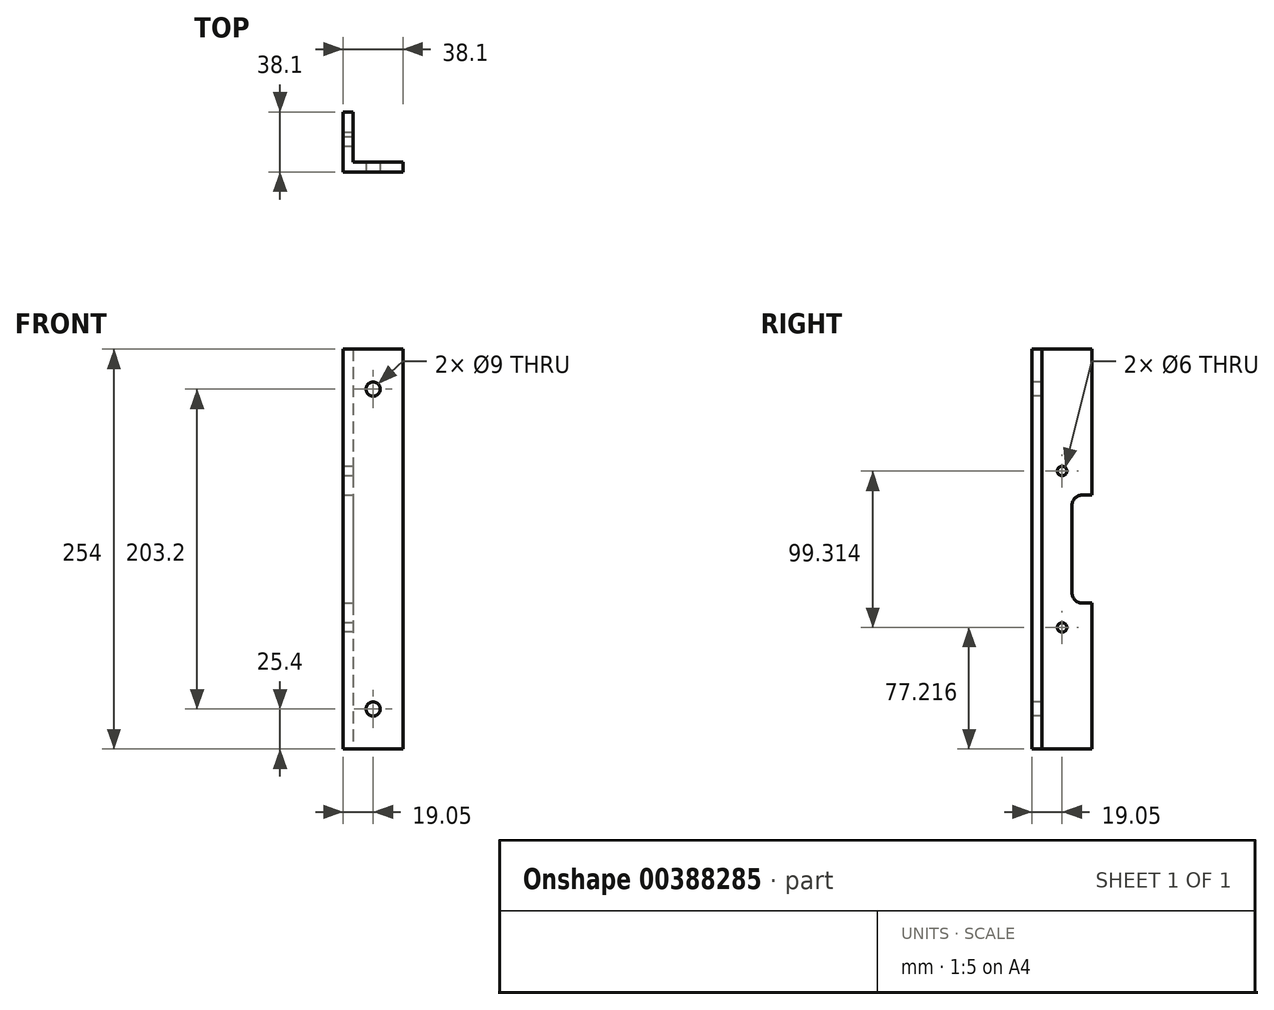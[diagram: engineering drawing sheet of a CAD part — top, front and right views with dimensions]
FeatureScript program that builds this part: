
annotation { "Feature Type Name" : "Feature", "Feature Type Description" : "" }
export const myFeature = defineFeature(function(context is Context, id is Id, definition is map)
    precondition{}
    {
        {
            var Q0;
            Q0=qCreatedBy(makeId("Top.planeOp"),FACE);
            var sketch = newSketch(context, id + "F0", { "sketchPlane" : qUnion([Q0])});
            skLineSegment(sketch, "E0", {"start": v(0, 0) * mm, "end": v(38.1, 0) * mm});
            skLineSegment(sketch, "E1", {"start": v(38.1, 0) * mm, "end": v(38.1, 6.35) * mm});
            skLineSegment(sketch, "E2", {"start": v(38.1, 6.35) * mm, "end": v(6.35, 6.35) * mm});
            skLineSegment(sketch, "E3", {"start": v(6.35, 6.35) * mm, "end": v(6.35, 38.1) * mm});
            skLineSegment(sketch, "E4", {"start": v(6.35, 38.1) * mm, "end": v(0, 38.1) * mm});
            skLineSegment(sketch, "E5", {"start": v(0, 38.1) * mm, "end": v(0, 0) * mm});
            skSolve(sketch);
        }
        {
            var Q0;
            Q0=makeQuery(id+"F0.imprint","IMPRINT",FACE,{"disambiguationData":[TD([[makeQuery(id+"F0.imprint","IMPRINT",EDGE,{"derivedFrom":sQuery(id+"F0.wireOp",EDGE,"E0")}),1.0]])]});
            extrude(context, id + "F1", {"entities" : qUnion([Q0]), "depth" : 254 * mm});
        }
        {
            var Q0;
            Q0=makeQuery(id+"F1.opExtrude","SWEPT_FACE",FACE,{"disambiguationData":[OSD([sQuery(id+"F0.wireOp",EDGE,"E0")])]});
            var sketch = newSketch(context, id + "F2", { "sketchPlane" : qUnion([Q0])});
            skLineSegment(sketch, "E6", {"start": v(19.05, 254) * mm, "end": v(19.05, 33.27) * mm, "construction": true});
            skPoint(sketch, "E7", {"position": v(19.05, 228.6) * mm});
            skPoint(sketch, "E8", {"position": v(19.05, 25.4) * mm});
            skSolve(sketch);
        }
        {
            var Q0;
            Q0=sQuery(id+"F2.wireOp",VERTEX,"E7");
            var Q1;
            Q1=makeQuery(id+"F1.opExtrude","SWEPT_BODY",BODY,{"disambiguationData":[OSD([sQuery(id+"F0.wireOp",EDGE,"E0"),sQuery(id+"F0.wireOp",EDGE,"E1"),sQuery(id+"F0.wireOp",EDGE,"E2"),sQuery(id+"F0.wireOp",EDGE,"E3"),sQuery(id+"F0.wireOp",EDGE,"E4"),sQuery(id+"F0.wireOp",EDGE,"E5")])]});
            hole(context, id + "F3", {"style" : HoleStyle.SIMPLE, "endStyle" : HoleEndStyle.THROUGH, "holeDiameter" : 9 * mm, "isTappedThrough" : true, "tappedDepth" : 12.7 * mm, "tapClearance" : 3, "locations" : qUnion([Q0]), "scope" : qUnion([Q1])});
        }
        {
            var Q0;
            Q0=sQuery(id+"F2.wireOp",VERTEX,"E8");
            var Q1;
            Q1=makeQuery(id+"F1.opExtrude","SWEPT_BODY",BODY,{"disambiguationData":[OSD([sQuery(id+"F0.wireOp",EDGE,"E0"),sQuery(id+"F0.wireOp",EDGE,"E1"),sQuery(id+"F0.wireOp",EDGE,"E2"),sQuery(id+"F0.wireOp",EDGE,"E3"),sQuery(id+"F0.wireOp",EDGE,"E4"),sQuery(id+"F0.wireOp",EDGE,"E5")])]});
            hole(context, id + "F4", {"style" : HoleStyle.SIMPLE, "endStyle" : HoleEndStyle.THROUGH, "holeDiameter" : 9 * mm, "isTappedThrough" : true, "tappedDepth" : 12.7 * mm, "tapClearance" : 3, "locations" : qUnion([Q0]), "scope" : qUnion([Q1])});
        }
        {
            var Q0;
            Q0=makeQuery(id+"F1.opExtrude","SWEPT_FACE",FACE,{"disambiguationData":[OSD([sQuery(id+"F0.wireOp",EDGE,"E5")])]});
            var sketch = newSketch(context, id + "F5", { "sketchPlane" : qUnion([Q0])});
            skLineSegment(sketch, "E9", {"start": v(-19.05, -96.16) * mm, "end": v(-19.05, 311.1) * mm, "construction": true});
            skSolve(sketch);
        }
        {
            var Q0;
            {var subQ0=sQuery(id+"F0.wireOp",EDGE,"E5");Q0=makeQuery(id+"F5.imprint","IMPRINT",FACE,{"disambiguationData":[TD([[makeQuery(id+"F5.imprint","IMPRINT",EDGE,{"derivedFrom":makeQuery(id+"F1.opExtrude","CAP_EDGE",EDGE,{"disambiguationData":[OSD([subQ0])],"isStart":true})}),1.0]])]});}
            var sketch = newSketch(context, id + "F6", { "sketchPlane" : qUnion([Q0])});
            skLineSegment(sketch, "E10", {"start": v(-46.64, 127) * mm, "end": v(0, 127) * mm});
            skSolve(sketch);
        }
        {
            var Q0;
            {var subQ0=sQuery(id+"F0.wireOp",EDGE,"E5");Q0=makeQuery(id+"F5.imprint","IMPRINT",FACE,{"disambiguationData":[TD([[makeQuery(id+"F5.imprint","IMPRINT",EDGE,{"derivedFrom":makeQuery(id+"F1.opExtrude","CAP_EDGE",EDGE,{"disambiguationData":[OSD([subQ0])],"isStart":true})}),1.0]])]});}
            var sketch = newSketch(context, id + "F7", { "sketchPlane" : qUnion([Q0])});
            skPoint(sketch, "E11", {"position": v(-19.05, 176.53) * mm});
            skSolve(sketch);
        }
        {
            var Q0;
            {var subQ0=sQuery(id+"F0.wireOp",EDGE,"E5");Q0=makeQuery(id+"F5.imprint","IMPRINT",FACE,{"disambiguationData":[TD([[makeQuery(id+"F5.imprint","IMPRINT",EDGE,{"derivedFrom":makeQuery(id+"F1.opExtrude","CAP_EDGE",EDGE,{"disambiguationData":[OSD([subQ0])],"isStart":true})}),1.0]])]});}
            var sketch = newSketch(context, id + "F8", { "sketchPlane" : qUnion([Q0])});
            skPoint(sketch, "E12", {"position": v(-19.05, 77.22) * mm});
            skSolve(sketch);
        }
        {
            var Q0;
            Q0=sQuery(id+"F8.wireOp",VERTEX,"E12");
            var Q1;
            Q1=sQuery(id+"F7.wireOp",VERTEX,"E11");
            var Q2;
            Q2=makeQuery(id+"F1.opExtrude","SWEPT_BODY",BODY,{"disambiguationData":[OSD([sQuery(id+"F0.wireOp",EDGE,"E0"),sQuery(id+"F0.wireOp",EDGE,"E1"),sQuery(id+"F0.wireOp",EDGE,"E2"),sQuery(id+"F0.wireOp",EDGE,"E3"),sQuery(id+"F0.wireOp",EDGE,"E4"),sQuery(id+"F0.wireOp",EDGE,"E5")])]});
            hole(context, id + "F9", {"style" : HoleStyle.SIMPLE, "endStyle" : HoleEndStyle.THROUGH, "holeDiameter" : 6 * mm, "isTappedThrough" : true, "tappedDepth" : 12.7 * mm, "tapClearance" : 3, "locations" : qUnion([Q0, Q1]), "scope" : qUnion([Q2])});
        }
        {
            var Q0;
            Q0=makeQuery(id+"F1.opExtrude","SWEPT_FACE",FACE,{"disambiguationData":[OSD([sQuery(id+"F0.wireOp",EDGE,"E3")])]});
            var sketch = newSketch(context, id + "F10", { "sketchPlane" : qUnion([Q0])});
            skLineSegment(sketch, "E13", {"start": v(25.4, 154.94) * mm, "end": v(25.4, 99.06) * mm});
            skLineSegment(sketch, "E14", {"start": v(38.1, 92.7) * mm, "end": v(38.1, 161.3) * mm});
            skLineSegment(sketch, "E15", {"start": v(38.1, 161.3) * mm, "end": v(31.75, 161.3) * mm});
            skLineSegment(sketch, "E16", {"start": v(31.75, 92.7) * mm, "end": v(38.1, 92.7) * mm});
            skArc(sketch, "E17.filletArc", {"start": v(31.75, 161.3) * mm, "mid": v(27.26, 159.43) * mm, "end": v(25.4, 154.94) * mm});
            skArc(sketch, "E18.filletArc", {"start": v(25.4, 99.06) * mm, "mid": v(27.26, 94.57) * mm, "end": v(31.75, 92.7) * mm});
            skSolve(sketch);
        }
        {
            var Q0;
            Q0 = qSketchRegion(id + "F10", true);
            extrude(context, id + "F11", {"entities" : qUnion([Q0]), "operationType" : NewBodyOperationType.REMOVE, "endBound" : BoundingType.UP_TO_NEXT, "oppositeDirection" : true, "depth" : 25.4 * mm, "offsetDistance" : 25.4 * mm});
        }
    });
